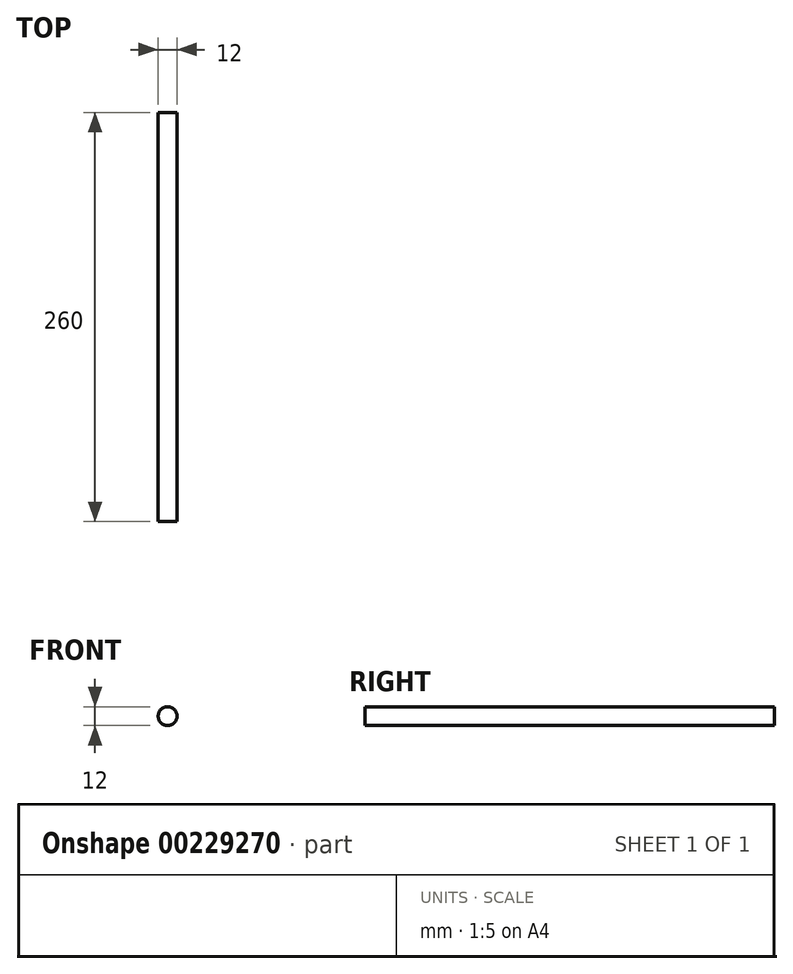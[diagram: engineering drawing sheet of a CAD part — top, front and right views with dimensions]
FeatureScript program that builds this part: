
annotation { "Feature Type Name" : "Feature", "Feature Type Description" : "" }
export const myFeature = defineFeature(function(context is Context, id is Id, definition is map)
    precondition{}
    {
        {
            var Q0;
            Q0=qCreatedBy(makeId("Front.planeOp"),FACE);
            var sketch = newSketch(context, id + "F0", { "sketchPlane" : qUnion([Q0])});
            skCircle(sketch, "E0", {"center": v(0, 0) * mm, "radius": 6 * mm});
            skSolve(sketch);
        }
        {
            var Q0;
            Q0=qSketchRegion(id+"F0",true);
            extrude(context, id + "F1", {"entities" : qUnion([Q0]), "depth" : 260 * mm});
        }
    });
